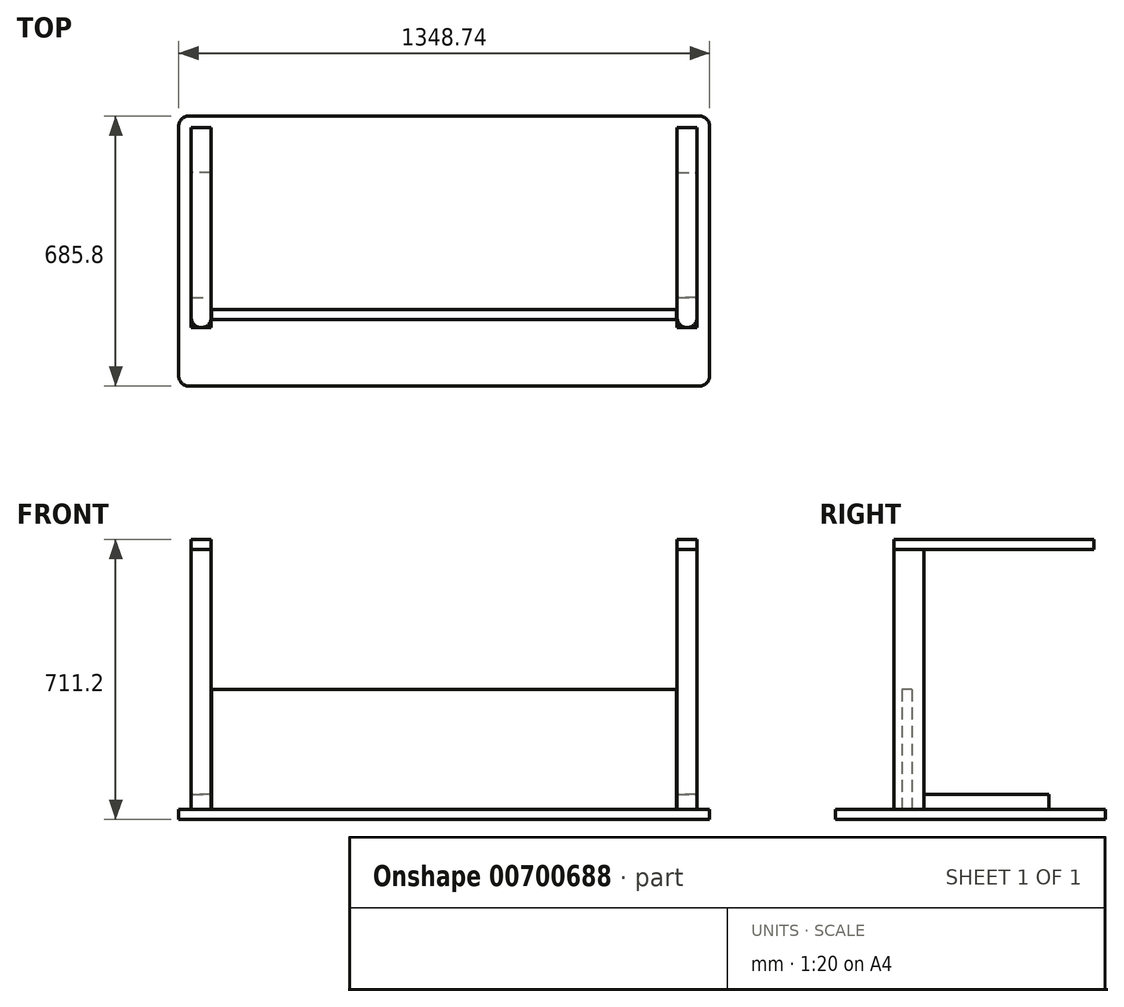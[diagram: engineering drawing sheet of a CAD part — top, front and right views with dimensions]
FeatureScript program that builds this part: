
annotation { "Feature Type Name" : "Feature", "Feature Type Description" : "" }
export const myFeature = defineFeature(function(context is Context, id is Id, definition is map)
    precondition{}
    {
        {
            var Q0;
            Q0=qCreatedBy(makeId("Top.planeOp"),FACE);
            var sketch = newSketch(context, id + "F0", { "sketchPlane" : qUnion([Q0])});
            skLineSegment(sketch, "E0.bottom", {"start": v(674.37, 342.9) * mm, "end": v(-674.37, 342.9) * mm});
            skLineSegment(sketch, "E0.top", {"start": v(674.37, -342.9) * mm, "end": v(-674.37, -342.9) * mm});
            skLineSegment(sketch, "E0.left", {"start": v(674.37, 342.9) * mm, "end": v(674.37, -342.9) * mm});
            skLineSegment(sketch, "E0.right", {"start": v(-674.37, 342.9) * mm, "end": v(-674.37, -342.9) * mm});
            skPoint(sketch, "E0.middle", {"position": v(0, 0) * mm});
            skSolve(sketch);
        }
        {
            var Q0;
            Q0=makeQuery(id+"F0.imprint","IMPRINT",FACE,{"disambiguationData":[TD([[makeQuery(id+"F0.imprint","IMPRINT",EDGE,{"derivedFrom":sQuery(id+"F0.wireOp",EDGE,"E0.bottom")}),1.0]])]});
            extrude(context, id + "F1", {"entities" : qUnion([Q0]), "depth" : 25.4 * mm, "offsetDistance" : 25.4 * mm});
        }
        {
            var Q0;
            Q0=makeQuery(id+"F1.opExtrude","CAP_FACE",FACE,{"disambiguationData":[OSD([sQuery(id+"F0.wireOp",EDGE,"E0.bottom"),sQuery(id+"F0.wireOp",EDGE,"E0.top"),sQuery(id+"F0.wireOp",EDGE,"E0.left"),sQuery(id+"F0.wireOp",EDGE,"E0.right")])],"isStart":false});
            var sketch = newSketch(context, id + "F2", { "sketchPlane" : qUnion([Q0])});
            skLineSegment(sketch, "E1", {"start": v(0, 0) * mm, "end": v(0, 342.9) * mm});
            skLineSegment(sketch, "E2", {"start": v(0, 0) * mm, "end": v(0, -342.9) * mm});
            skSolve(sketch);
        }
        {
            var Q0;
            {var subQ3=sQuery(id+"F2.wireOp",EDGE,"E1");Q0=makeQuery(id+"F2.imprint","IMPRINT",FACE,{"disambiguationData":[TD([[makeQuery(id+"F2.imprint","IMPRINT",EDGE,{"derivedFrom":subQ3}),1.0]])]});}
            var sketch = newSketch(context, id + "F3", { "sketchPlane" : qUnion([Q0])});
            skSolve(sketch);
        }
        {
            var Q0;
            {var subQ2=sQuery(id+"F2.wireOp",EDGE,"E1");Q0=makeQuery(id+"F3.imprint","IMPRINT",FACE,{"disambiguationData":[TD([[makeQuery(id+"F3.imprint","IMPRINT",EDGE,{"derivedFrom":makeQuery(id+"F2.imprint","IMPRINT",EDGE,{"derivedFrom":subQ2})}),1.0]])]});}
            var sketch = newSketch(context, id + "F4", { "sketchPlane" : qUnion([Q0])});
            skLineSegment(sketch, "E3", {"start": v(-642.51, 199.13) * mm, "end": v(-642.51, -118.37) * mm});
            skLineSegment(sketch, "E4", {"start": v(-642.51, -118.37) * mm, "end": v(-591.71, -118.37) * mm});
            skLineSegment(sketch, "E5", {"start": v(-591.71, -118.37) * mm, "end": v(-591.71, 199.13) * mm});
            skLineSegment(sketch, "E6", {"start": v(-591.71, 199.13) * mm, "end": v(-642.51, 199.13) * mm});
            skLineSegment(sketch, "E7.MirrorCS", {"start": v(591.71, -118.37) * mm, "end": v(591.71, 199.13) * mm});
            skLineSegment(sketch, "E8.MirrorCS", {"start": v(642.51, 199.13) * mm, "end": v(642.51, -118.37) * mm});
            skLineSegment(sketch, "E9.MirrorCS", {"start": v(642.51, -118.37) * mm, "end": v(591.71, -118.37) * mm});
            skLineSegment(sketch, "E10", {"start": v(591.71, 199.13) * mm, "end": v(642.51, 199.13) * mm});
            skSolve(sketch);
        }
        {
            var Q0;
            Q0=makeQuery(id+"F4.imprint","IMPRINT",FACE,{"disambiguationData":[TD([[makeQuery(id+"F4.imprint","IMPRINT",EDGE,{"derivedFrom":sQuery(id+"F4.wireOp",EDGE,"E3")}),1.0]])]});
            var Q1;
            Q1=makeQuery(id+"F4.imprint","IMPRINT",FACE,{"disambiguationData":[TD([[makeQuery(id+"F4.imprint","IMPRINT",EDGE,{"derivedFrom":sQuery(id+"F4.wireOp",EDGE,"E7.MirrorCS")}),-1.0]])]});
            extrude(context, id + "F5", {"entities" : qUnion([Q0, Q1]), "operationType" : NewBodyOperationType.ADD, "depth" : 38.1 * mm, "offsetDistance" : 25.4 * mm});
        }
        {
            var Q0;
            {var subQ3=sQuery(id+"F2.wireOp",EDGE,"E1");Q0=makeQuery(id+"F2.imprint","IMPRINT",FACE,{"disambiguationData":[TD([[makeQuery(id+"F2.imprint","IMPRINT",EDGE,{"derivedFrom":subQ3}),1.0]])]});}
            var sketch = newSketch(context, id + "F6", { "sketchPlane" : qUnion([Q0])});
            skLineSegment(sketch, "E11.bottom", {"start": v(-642.52, -118.37) * mm, "end": v(-591.72, -118.37) * mm});
            skLineSegment(sketch, "E11.top", {"start": v(-642.52, -194.57) * mm, "end": v(-591.72, -194.57) * mm});
            skLineSegment(sketch, "E11.left", {"start": v(-642.52, -118.37) * mm, "end": v(-642.52, -194.57) * mm});
            skLineSegment(sketch, "E11.right", {"start": v(-591.72, -118.37) * mm, "end": v(-591.72, -194.57) * mm});
            skSolve(sketch);
        }
        {
            var Q0;
            Q0=makeQuery(id+"F6.imprint","IMPRINT",FACE,{"disambiguationData":[TD([[makeQuery(id+"F6.imprint","IMPRINT",EDGE,{"derivedFrom":sQuery(id+"F6.wireOp",EDGE,"E11.bottom")}),-1.0]])]});
            extrude(context, id + "F7", {"entities" : qUnion([Q0]), "operationType" : NewBodyOperationType.ADD, "depth" : 660.4 * mm, "offsetDistance" : 25.4 * mm});
        }
        {
            var Q0;
            {var subQ2=sQuery(id+"F2.wireOp",EDGE,"E1");Q0=makeQuery(id+"F2.imprint","IMPRINT",FACE,{"disambiguationData":[TD([[makeQuery(id+"F2.imprint","IMPRINT",EDGE,{"derivedFrom":subQ2}),-1.0]])]});}
            var sketch = newSketch(context, id + "F8", { "sketchPlane" : qUnion([Q0])});
            skLineSegment(sketch, "E12.bottom", {"start": v(591.6, -118.52) * mm, "end": v(642.4, -118.52) * mm});
            skLineSegment(sketch, "E12.top", {"start": v(591.6, -194.72) * mm, "end": v(642.4, -194.72) * mm});
            skLineSegment(sketch, "E12.left", {"start": v(591.6, -118.52) * mm, "end": v(591.6, -194.72) * mm});
            skLineSegment(sketch, "E12.right", {"start": v(642.4, -118.52) * mm, "end": v(642.4, -194.72) * mm});
            skSolve(sketch);
        }
        {
            var Q0;
            Q0=makeQuery(id+"F8.imprint","IMPRINT",FACE,{"disambiguationData":[TD([[makeQuery(id+"F8.imprint","IMPRINT",EDGE,{"derivedFrom":sQuery(id+"F8.wireOp",EDGE,"E12.bottom")}),-1.0]])]});
            extrude(context, id + "F9", {"entities" : qUnion([Q0]), "operationType" : NewBodyOperationType.ADD, "depth" : 660.4 * mm, "offsetDistance" : 25.4 * mm});
        }
        {
            var Q0;
            Q0=makeQuery(id+"F7.opExtrude","CAP_FACE",FACE,{"disambiguationData":[OSD([sQuery(id+"F6.wireOp",EDGE,"E11.bottom"),sQuery(id+"F6.wireOp",EDGE,"E11.top"),sQuery(id+"F6.wireOp",EDGE,"E11.left"),sQuery(id+"F6.wireOp",EDGE,"E11.right")])],"isStart":false});
            var sketch = newSketch(context, id + "F10", { "sketchPlane" : qUnion([Q0])});
            skLineSegment(sketch, "E13.bottom", {"start": v(-617.12, -194.57) * mm, "end": v(-617.12, -194.57) * mm});
            skLineSegment(sketch, "E13.top", {"start": v(-642.52, 313.43) * mm, "end": v(-591.72, 313.43) * mm});
            skLineSegment(sketch, "E13.left", {"start": v(-642.52, -169.17) * mm, "end": v(-642.52, 313.43) * mm});
            skLineSegment(sketch, "E13.right", {"start": v(-591.72, -169.17) * mm, "end": v(-591.72, 313.43) * mm});
            skPoint(sketch, "E14.visualSharp", {"position": v(-591.72, -194.57) * mm});
            skArc(sketch, "E14.filletArc", {"start": v(-617.12, -194.57) * mm, "mid": v(-599.16, -187.13) * mm, "end": v(-591.72, -169.17) * mm});
            skPoint(sketch, "E15.visualSharp", {"position": v(-642.52, -194.57) * mm});
            skArc(sketch, "E15.filletArc", {"start": v(-642.52, -169.17) * mm, "mid": v(-635.08, -187.13) * mm, "end": v(-617.12, -194.57) * mm});
            skLineSegment(sketch, "E16.MirrorCS", {"start": v(591.72, -169.17) * mm, "end": v(591.72, 313.43) * mm});
            skLineSegment(sketch, "E17.MirrorCS", {"start": v(642.52, -169.17) * mm, "end": v(642.52, 313.43) * mm});
            skArc(sketch, "E18.MirrorCS", {"start": v(617.12, -194.57) * mm, "mid": v(599.16, -187.13) * mm, "end": v(591.72, -169.17) * mm});
            skArc(sketch, "E19.MirrorCS", {"start": v(642.52, -169.17) * mm, "mid": v(635.08, -187.13) * mm, "end": v(617.12, -194.57) * mm});
            skLineSegment(sketch, "E20", {"start": v(591.72, 313.43) * mm, "end": v(642.52, 313.43) * mm});
            skSolve(sketch);
        }
        {
            var Q0;
            Q0=makeQuery(id+"F10.imprint","IMPRINT",FACE,{"disambiguationData":[TD([[makeQuery(id+"F10.imprint","IMPRINT",EDGE,{"derivedFrom":sQuery(id+"F10.wireOp",EDGE,"E16.MirrorCS")}),-1.0]])]});
            var Q1;
            {var subQ1=sQuery(id+"F10.wireOp",EDGE,"E14.filletArc");Q1=makeQuery(id+"F10.imprint","IMPRINT",FACE,{"disambiguationData":[TD([[makeQuery(id+"F10.imprint","IMPRINT",EDGE,{"derivedFrom":subQ1}),1.0]])]});}
            var Q2;
            {var subQ0=sQuery(id+"F10.wireOp",EDGE,"E13.top");Q2=makeQuery(id+"F10.imprint","IMPRINT",FACE,{"disambiguationData":[TD([[makeQuery(id+"F10.imprint","IMPRINT",EDGE,{"derivedFrom":subQ0}),-1.0]])]});}
            extrude(context, id + "F11", {"entities" : qUnion([Q0, Q1, Q2]), "operationType" : NewBodyOperationType.ADD, "depth" : 25.4 * mm, "offsetDistance" : 25.4 * mm});
        }
        {
            var Q0;
            {var subQ3=sQuery(id+"F2.wireOp",EDGE,"E1");Q0=makeQuery(id+"F2.imprint","IMPRINT",FACE,{"disambiguationData":[TD([[makeQuery(id+"F2.imprint","IMPRINT",EDGE,{"derivedFrom":subQ3}),1.0]])]});}
            var sketch = newSketch(context, id + "F12", { "sketchPlane" : qUnion([Q0])});
            skLineSegment(sketch, "E21.bottom", {"start": v(-590.36, -149.01) * mm, "end": v(590.36, -149.01) * mm});
            skLineSegment(sketch, "E21.top", {"start": v(-590.36, -174.41) * mm, "end": v(590.36, -174.41) * mm});
            skLineSegment(sketch, "E21.left", {"start": v(-590.36, -149.01) * mm, "end": v(-590.36, -174.41) * mm});
            skLineSegment(sketch, "E21.right", {"start": v(590.36, -149.01) * mm, "end": v(590.36, -174.41) * mm});
            skSolve(sketch);
        }
        {
            var Q0;
            Q0 = qSketchRegion(id + "F12", true);
            extrude(context, id + "F13", {"entities" : qUnion([Q0]), "operationType" : NewBodyOperationType.ADD, "depth" : 304.8 * mm, "offsetDistance" : 25.4 * mm});
        }
        {
            var Q0;
            Q0=makeQuery(id+"F1.opExtrude","SWEPT_EDGE",EDGE,{"disambiguationData":[OSD([sQuery(id+"F0.wireOp",EDGE,"E0.bottom"),sQuery(id+"F0.wireOp",EDGE,"E0.left")])]});
            var Q1;
            Q1=makeQuery(id+"F1.opExtrude","SWEPT_EDGE",EDGE,{"disambiguationData":[OSD([sQuery(id+"F0.wireOp",EDGE,"E0.bottom"),sQuery(id+"F0.wireOp",EDGE,"E0.right")])]});
            var Q2;
            Q2=makeQuery(id+"F1.opExtrude","SWEPT_EDGE",EDGE,{"disambiguationData":[OSD([sQuery(id+"F0.wireOp",EDGE,"E0.top"),sQuery(id+"F0.wireOp",EDGE,"E0.left")])]});
            fillet(context, id + "F14", {"entities" : qUnion([Q0, Q1, Q2]), "radius" : 25.4 * mm, "tangentPropagation" : true, "allowEdgeOverflow" : false});
        }
        {
            var Q0;
            Q0=makeQuery(id+"F1.opExtrude","SWEPT_EDGE",EDGE,{"disambiguationData":[OSD([sQuery(id+"F0.wireOp",EDGE,"E0.top"),sQuery(id+"F0.wireOp",EDGE,"E0.right")])]});
            fillet(context, id + "F15", {"entities" : qUnion([Q0]), "radius" : 25.4 * mm, "tangentPropagation" : true, "allowEdgeOverflow" : false});
        }
    });
